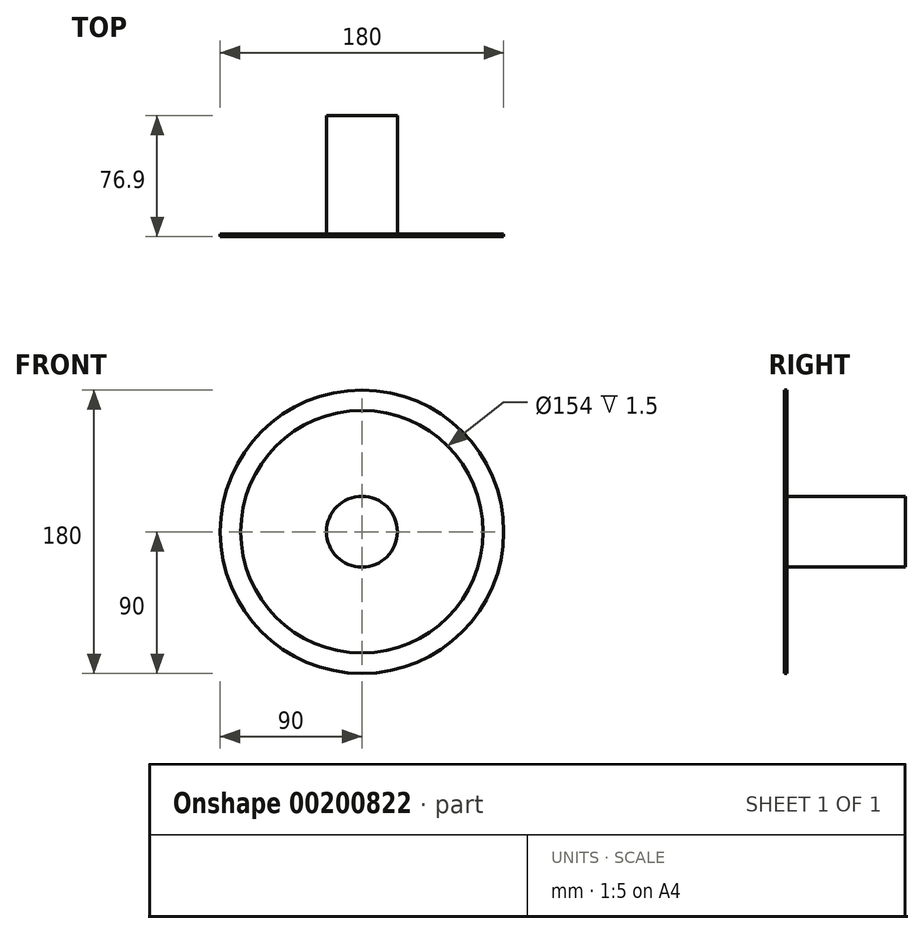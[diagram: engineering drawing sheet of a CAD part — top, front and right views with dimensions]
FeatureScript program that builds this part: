
annotation { "Feature Type Name" : "Feature", "Feature Type Description" : "" }
export const myFeature = defineFeature(function(context is Context, id is Id, definition is map)
    precondition{}
    {
        {
            var Q0;
            Q0=qCreatedBy(makeId("Front.planeOp"),FACE);
            var sketch = newSketch(context, id + "F0", { "sketchPlane" : qUnion([Q0])});
            skCircle(sketch, "E0", {"center": v(0, 0) * mm, "radius": 90 * mm});
            skCircle(sketch, "E1", {"center": v(0, 0) * mm, "radius": 77 * mm});
            skSolve(sketch);
        }
        {
            var Q0;
            Q0=makeQuery(id+"F0.imprint","IMPRINT",FACE,{"disambiguationData":[TD([[makeQuery(id+"F0.imprint","IMPRINT",EDGE,{"derivedFrom":sQuery(id+"F0.wireOp",EDGE,"E0")}),1.0]])]});
            extrude(context, id + "F1", {"entities" : qUnion([Q0]), "depth" : 1.5 * mm});
        }
        {
            var Q0;
            Q0=qCreatedBy(makeId("Front.planeOp"),FACE);
            var sketch = newSketch(context, id + "F2", { "sketchPlane" : qUnion([Q0])});
            skCircle(sketch, "E2", {"center": v(0, 0) * mm, "radius": 22.5 * mm});
            skSolve(sketch);
        }
        {
            var Q0;
            Q0=makeQuery(id+"F2.imprint","IMPRINT",FACE,{"disambiguationData":[TD([[makeQuery(id+"F2.imprint","IMPRINT",EDGE,{"derivedFrom":sQuery(id+"F2.wireOp",EDGE,"E2")}),1.0]])]});
            extrude(context, id + "F3", {"entities" : qUnion([Q0]), "oppositeDirection" : true, "depth" : 75.4 * mm});
        }
    });
